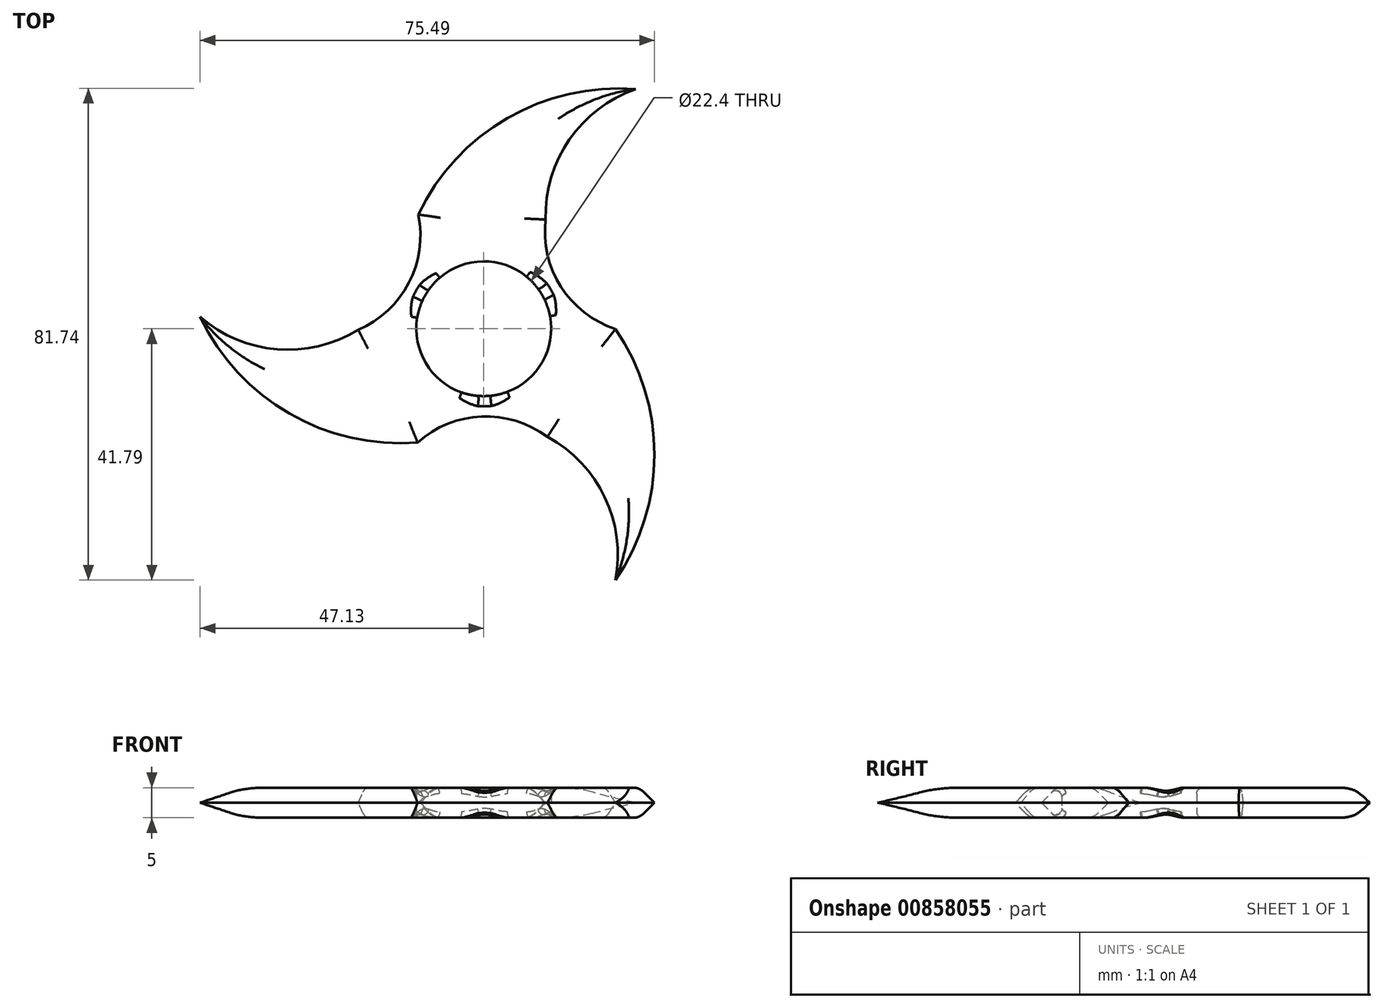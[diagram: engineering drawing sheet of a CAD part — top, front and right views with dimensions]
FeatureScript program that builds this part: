
annotation { "Feature Type Name" : "Feature", "Feature Type Description" : "" }
export const myFeature = defineFeature(function(context is Context, id is Id, definition is map)
    precondition{}
    {
        {
            var Q0;
            Q0=qCreatedBy(makeId("Top.planeOp"),FACE);
            var sketch = newSketch(context, id + "F0", { "sketchPlane" : qUnion([Q0])});
            skCircle(sketch, "E0", {"center": v(0, 0) * mm, "radius": 11.2 * mm});
            skArc(sketch, "E1", {"start": v(10.29, 18.16) * mm, "mid": v(12.82, 6.98) * mm, "end": v(21.87, -0.05) * mm});
            skArc(sketch, "E2.1.0", {"start": v(-20.87, -0.17) * mm, "mid": v(-12.45, 7.61) * mm, "end": v(-10.9, 18.97) * mm});
            skArc(sketch, "E2.2.0", {"start": v(10.58, -17.99) * mm, "mid": v(-0.37, -14.6) * mm, "end": v(-10.98, -18.92) * mm});
            skArc(sketch, "E3", {"start": v(21.87, -41.8) * mm, "mid": v(28.36, -20.92) * mm, "end": v(21.87, -0.05) * mm});
            skArc(sketch, "E4", {"start": v(21.87, -41.8) * mm, "mid": v(20.12, -28.04) * mm, "end": v(10.58, -17.99) * mm});
            skPoint(sketch, "E5.center.orphan", {"position": v(0, 26.43) * mm});
            skArc(sketch, "E6.1.0", {"start": v(25.26, 39.84) * mm, "mid": v(3.94, 35.02) * mm, "end": v(-10.9, 18.97) * mm});
            skArc(sketch, "E6.1.1", {"start": v(25.26, 39.84) * mm, "mid": v(14.22, 31.45) * mm, "end": v(10.29, 18.16) * mm});
            skArc(sketch, "E6.2.0", {"start": v(-47.13, 1.95) * mm, "mid": v(-32.3, -14.1) * mm, "end": v(-10.98, -18.92) * mm});
            skArc(sketch, "E6.2.1", {"start": v(-47.13, 1.95) * mm, "mid": v(-34.35, -3.4) * mm, "end": v(-20.87, -0.17) * mm});
            skSolve(sketch);
        }
        {
            var Q0;
            Q0 = qSketchRegion(id + "F0", true);
            extrude(context, id + "F1", {"entities" : qUnion([Q0]), "depth" : 2.5 * mm, "offsetDistance" : 25 * mm, "hasSecondDirection" : true, "secondDirectionOppositeDirection" : true, "secondDirectionDepth" : 2.5 * mm});
        }
        {
            var Q0;
            Q0=makeQuery(id+"F1.opExtrude","CAP_EDGE",EDGE,{"disambiguationData":[OSD([sQuery(id+"F0.wireOp",EDGE,"E3")])],"isStart":false});
            var Q1;
            Q1=makeQuery(id+"F1.opExtrude","CAP_EDGE",EDGE,{"disambiguationData":[OSD([sQuery(id+"F0.wireOp",EDGE,"E6.1.1")])],"isStart":false});
            var Q2;
            Q2=makeQuery(id+"F1.opExtrude","CAP_EDGE",EDGE,{"disambiguationData":[OSD([sQuery(id+"F0.wireOp",EDGE,"E6.1.0")])],"isStart":false});
            var Q3;
            Q3=makeQuery(id+"F1.opExtrude","CAP_EDGE",EDGE,{"disambiguationData":[OSD([sQuery(id+"F0.wireOp",EDGE,"E1")])],"isStart":false});
            var Q4;
            Q4=makeQuery(id+"F1.opExtrude","CAP_EDGE",EDGE,{"disambiguationData":[OSD([sQuery(id+"F0.wireOp",EDGE,"E2.2.0")])],"isStart":false});
            var Q5;
            Q5=makeQuery(id+"F1.opExtrude","CAP_EDGE",EDGE,{"disambiguationData":[OSD([sQuery(id+"F0.wireOp",EDGE,"E4")])],"isStart":false});
            var Q6;
            Q6=makeQuery(id+"F1.opExtrude","CAP_EDGE",EDGE,{"disambiguationData":[OSD([sQuery(id+"F0.wireOp",EDGE,"E6.2.1")])],"isStart":false});
            var Q7;
            Q7=makeQuery(id+"F1.opExtrude","CAP_EDGE",EDGE,{"disambiguationData":[OSD([sQuery(id+"F0.wireOp",EDGE,"E2.1.0")])],"isStart":false});
            var Q8;
            Q8=makeQuery(id+"F1.opExtrude","CAP_EDGE",EDGE,{"disambiguationData":[OSD([sQuery(id+"F0.wireOp",EDGE,"E6.2.0")])],"isStart":false});
            chamfer(context, id + "F2", {"entities" : qUnion([Q0, Q1, Q2, Q3, Q4, Q5, Q6, Q7, Q8]), "width" : 2.5 * mm, "tangentPropagation" : true});
        }
        {
            var Q0;
            Q0=makeQuery(id+"F1.opExtrude","CAP_EDGE",EDGE,{"disambiguationData":[OSD([sQuery(id+"F0.wireOp",EDGE,"E6.2.0")])],"isStart":true});
            var Q1;
            Q1=makeQuery(id+"F1.opExtrude","CAP_EDGE",EDGE,{"disambiguationData":[OSD([sQuery(id+"F0.wireOp",EDGE,"E2.2.0")])],"isStart":true});
            var Q2;
            Q2=makeQuery(id+"F1.opExtrude","CAP_EDGE",EDGE,{"disambiguationData":[OSD([sQuery(id+"F0.wireOp",EDGE,"E4")])],"isStart":true});
            var Q3;
            Q3=makeQuery(id+"F1.opExtrude","CAP_EDGE",EDGE,{"disambiguationData":[OSD([sQuery(id+"F0.wireOp",EDGE,"E3")])],"isStart":true});
            var Q4;
            Q4=makeQuery(id+"F1.opExtrude","CAP_EDGE",EDGE,{"disambiguationData":[OSD([sQuery(id+"F0.wireOp",EDGE,"E1")])],"isStart":true});
            var Q5;
            Q5=makeQuery(id+"F1.opExtrude","CAP_EDGE",EDGE,{"disambiguationData":[OSD([sQuery(id+"F0.wireOp",EDGE,"E6.1.1")])],"isStart":true});
            var Q6;
            Q6=makeQuery(id+"F1.opExtrude","CAP_EDGE",EDGE,{"disambiguationData":[OSD([sQuery(id+"F0.wireOp",EDGE,"E6.1.0")])],"isStart":true});
            var Q7;
            Q7=makeQuery(id+"F1.opExtrude","CAP_EDGE",EDGE,{"disambiguationData":[OSD([sQuery(id+"F0.wireOp",EDGE,"E2.1.0")])],"isStart":true});
            var Q8;
            Q8=makeQuery(id+"F1.opExtrude","CAP_EDGE",EDGE,{"disambiguationData":[OSD([sQuery(id+"F0.wireOp",EDGE,"E6.2.1")])],"isStart":true});
            chamfer(context, id + "F3", {"entities" : qUnion([Q0, Q1, Q2, Q3, Q4, Q5, Q6, Q7, Q8]), "width" : 2.5 * mm, "tangentPropagation" : true});
        }
        {
            var Q0;
            {var subQ0=sQuery(id+"F0.wireOp",EDGE,"E6.2.0");Q0=makeQuery(id+"F3.opChamfer","BLEND_EDGE",EDGE,{"blendedFrom":[makeQuery(id+"F1.opExtrude","CAP_EDGE",EDGE,{"disambiguationData":[OSD([subQ0])],"isStart":true}),makeQuery(id+"F1.opExtrude","CAP_FACE",FACE,{"disambiguationData":[OSD([sQuery(id+"F0.wireOp",EDGE,"E0"),sQuery(id+"F0.wireOp",EDGE,"E1"),sQuery(id+"F0.wireOp",EDGE,"E2.1.0"),sQuery(id+"F0.wireOp",EDGE,"E2.2.0"),sQuery(id+"F0.wireOp",EDGE,"E3"),sQuery(id+"F0.wireOp",EDGE,"E4"),sQuery(id+"F0.wireOp",EDGE,"E6.1.0"),sQuery(id+"F0.wireOp",EDGE,"E6.1.1"),subQ0,sQuery(id+"F0.wireOp",EDGE,"E6.2.1")])],"isStart":true})],"blendedInto":[makeQuery(id+"F1.opExtrude","CAP_FACE",FACE,{"disambiguationData":[OSD([sQuery(id+"F0.wireOp",EDGE,"E0"),sQuery(id+"F0.wireOp",EDGE,"E1"),sQuery(id+"F0.wireOp",EDGE,"E2.1.0"),sQuery(id+"F0.wireOp",EDGE,"E2.2.0"),sQuery(id+"F0.wireOp",EDGE,"E3"),sQuery(id+"F0.wireOp",EDGE,"E4"),sQuery(id+"F0.wireOp",EDGE,"E6.1.0"),sQuery(id+"F0.wireOp",EDGE,"E6.1.1"),subQ0,sQuery(id+"F0.wireOp",EDGE,"E6.2.1")])],"isStart":true})]});}
            var Q1;
            {var subQ0=sQuery(id+"F0.wireOp",EDGE,"E6.2.1");Q1=makeQuery(id+"F3.opChamfer","BLEND_EDGE",EDGE,{"blendedFrom":[makeQuery(id+"F1.opExtrude","CAP_EDGE",EDGE,{"disambiguationData":[OSD([subQ0])],"isStart":true}),makeQuery(id+"F1.opExtrude","CAP_FACE",FACE,{"disambiguationData":[OSD([sQuery(id+"F0.wireOp",EDGE,"E0"),sQuery(id+"F0.wireOp",EDGE,"E1"),sQuery(id+"F0.wireOp",EDGE,"E2.1.0"),sQuery(id+"F0.wireOp",EDGE,"E2.2.0"),sQuery(id+"F0.wireOp",EDGE,"E3"),sQuery(id+"F0.wireOp",EDGE,"E4"),sQuery(id+"F0.wireOp",EDGE,"E6.1.0"),sQuery(id+"F0.wireOp",EDGE,"E6.1.1"),sQuery(id+"F0.wireOp",EDGE,"E6.2.0"),subQ0])],"isStart":true})],"blendedInto":[makeQuery(id+"F1.opExtrude","CAP_FACE",FACE,{"disambiguationData":[OSD([sQuery(id+"F0.wireOp",EDGE,"E0"),sQuery(id+"F0.wireOp",EDGE,"E1"),sQuery(id+"F0.wireOp",EDGE,"E2.1.0"),sQuery(id+"F0.wireOp",EDGE,"E2.2.0"),sQuery(id+"F0.wireOp",EDGE,"E3"),sQuery(id+"F0.wireOp",EDGE,"E4"),sQuery(id+"F0.wireOp",EDGE,"E6.1.0"),sQuery(id+"F0.wireOp",EDGE,"E6.1.1"),sQuery(id+"F0.wireOp",EDGE,"E6.2.0"),subQ0])],"isStart":true})]});}
            var Q2;
            {var subQ0=sQuery(id+"F0.wireOp",EDGE,"E2.1.0");Q2=makeQuery(id+"F3.opChamfer","BLEND_EDGE",EDGE,{"blendedFrom":[makeQuery(id+"F1.opExtrude","CAP_EDGE",EDGE,{"disambiguationData":[OSD([subQ0])],"isStart":true}),makeQuery(id+"F1.opExtrude","CAP_FACE",FACE,{"disambiguationData":[OSD([sQuery(id+"F0.wireOp",EDGE,"E0"),sQuery(id+"F0.wireOp",EDGE,"E1"),subQ0,sQuery(id+"F0.wireOp",EDGE,"E2.2.0"),sQuery(id+"F0.wireOp",EDGE,"E3"),sQuery(id+"F0.wireOp",EDGE,"E4"),sQuery(id+"F0.wireOp",EDGE,"E6.1.0"),sQuery(id+"F0.wireOp",EDGE,"E6.1.1"),sQuery(id+"F0.wireOp",EDGE,"E6.2.0"),sQuery(id+"F0.wireOp",EDGE,"E6.2.1")])],"isStart":true})],"blendedInto":[makeQuery(id+"F1.opExtrude","CAP_FACE",FACE,{"disambiguationData":[OSD([sQuery(id+"F0.wireOp",EDGE,"E0"),sQuery(id+"F0.wireOp",EDGE,"E1"),subQ0,sQuery(id+"F0.wireOp",EDGE,"E2.2.0"),sQuery(id+"F0.wireOp",EDGE,"E3"),sQuery(id+"F0.wireOp",EDGE,"E4"),sQuery(id+"F0.wireOp",EDGE,"E6.1.0"),sQuery(id+"F0.wireOp",EDGE,"E6.1.1"),sQuery(id+"F0.wireOp",EDGE,"E6.2.0"),sQuery(id+"F0.wireOp",EDGE,"E6.2.1")])],"isStart":true})]});}
            var Q3;
            {var subQ0=sQuery(id+"F0.wireOp",EDGE,"E2.2.0");Q3=makeQuery(id+"F3.opChamfer","BLEND_EDGE",EDGE,{"blendedFrom":[makeQuery(id+"F1.opExtrude","CAP_EDGE",EDGE,{"disambiguationData":[OSD([subQ0])],"isStart":true}),makeQuery(id+"F1.opExtrude","CAP_FACE",FACE,{"disambiguationData":[OSD([sQuery(id+"F0.wireOp",EDGE,"E0"),sQuery(id+"F0.wireOp",EDGE,"E1"),sQuery(id+"F0.wireOp",EDGE,"E2.1.0"),subQ0,sQuery(id+"F0.wireOp",EDGE,"E3"),sQuery(id+"F0.wireOp",EDGE,"E4"),sQuery(id+"F0.wireOp",EDGE,"E6.1.0"),sQuery(id+"F0.wireOp",EDGE,"E6.1.1"),sQuery(id+"F0.wireOp",EDGE,"E6.2.0"),sQuery(id+"F0.wireOp",EDGE,"E6.2.1")])],"isStart":true})],"blendedInto":[makeQuery(id+"F1.opExtrude","CAP_FACE",FACE,{"disambiguationData":[OSD([sQuery(id+"F0.wireOp",EDGE,"E0"),sQuery(id+"F0.wireOp",EDGE,"E1"),sQuery(id+"F0.wireOp",EDGE,"E2.1.0"),subQ0,sQuery(id+"F0.wireOp",EDGE,"E3"),sQuery(id+"F0.wireOp",EDGE,"E4"),sQuery(id+"F0.wireOp",EDGE,"E6.1.0"),sQuery(id+"F0.wireOp",EDGE,"E6.1.1"),sQuery(id+"F0.wireOp",EDGE,"E6.2.0"),sQuery(id+"F0.wireOp",EDGE,"E6.2.1")])],"isStart":true})]});}
            var Q4;
            {var subQ0=sQuery(id+"F0.wireOp",EDGE,"E4");Q4=makeQuery(id+"F3.opChamfer","BLEND_EDGE",EDGE,{"blendedFrom":[makeQuery(id+"F1.opExtrude","CAP_EDGE",EDGE,{"disambiguationData":[OSD([subQ0])],"isStart":true}),makeQuery(id+"F1.opExtrude","CAP_FACE",FACE,{"disambiguationData":[OSD([sQuery(id+"F0.wireOp",EDGE,"E0"),sQuery(id+"F0.wireOp",EDGE,"E1"),sQuery(id+"F0.wireOp",EDGE,"E2.1.0"),sQuery(id+"F0.wireOp",EDGE,"E2.2.0"),sQuery(id+"F0.wireOp",EDGE,"E3"),subQ0,sQuery(id+"F0.wireOp",EDGE,"E6.1.0"),sQuery(id+"F0.wireOp",EDGE,"E6.1.1"),sQuery(id+"F0.wireOp",EDGE,"E6.2.0"),sQuery(id+"F0.wireOp",EDGE,"E6.2.1")])],"isStart":true})],"blendedInto":[makeQuery(id+"F1.opExtrude","CAP_FACE",FACE,{"disambiguationData":[OSD([sQuery(id+"F0.wireOp",EDGE,"E0"),sQuery(id+"F0.wireOp",EDGE,"E1"),sQuery(id+"F0.wireOp",EDGE,"E2.1.0"),sQuery(id+"F0.wireOp",EDGE,"E2.2.0"),sQuery(id+"F0.wireOp",EDGE,"E3"),subQ0,sQuery(id+"F0.wireOp",EDGE,"E6.1.0"),sQuery(id+"F0.wireOp",EDGE,"E6.1.1"),sQuery(id+"F0.wireOp",EDGE,"E6.2.0"),sQuery(id+"F0.wireOp",EDGE,"E6.2.1")])],"isStart":true})]});}
            var Q5;
            {var subQ0=sQuery(id+"F0.wireOp",EDGE,"E3");Q5=makeQuery(id+"F3.opChamfer","BLEND_EDGE",EDGE,{"blendedFrom":[makeQuery(id+"F1.opExtrude","CAP_EDGE",EDGE,{"disambiguationData":[OSD([subQ0])],"isStart":true}),makeQuery(id+"F1.opExtrude","CAP_FACE",FACE,{"disambiguationData":[OSD([sQuery(id+"F0.wireOp",EDGE,"E0"),sQuery(id+"F0.wireOp",EDGE,"E1"),sQuery(id+"F0.wireOp",EDGE,"E2.1.0"),sQuery(id+"F0.wireOp",EDGE,"E2.2.0"),subQ0,sQuery(id+"F0.wireOp",EDGE,"E4"),sQuery(id+"F0.wireOp",EDGE,"E6.1.0"),sQuery(id+"F0.wireOp",EDGE,"E6.1.1"),sQuery(id+"F0.wireOp",EDGE,"E6.2.0"),sQuery(id+"F0.wireOp",EDGE,"E6.2.1")])],"isStart":true})],"blendedInto":[makeQuery(id+"F1.opExtrude","CAP_FACE",FACE,{"disambiguationData":[OSD([sQuery(id+"F0.wireOp",EDGE,"E0"),sQuery(id+"F0.wireOp",EDGE,"E1"),sQuery(id+"F0.wireOp",EDGE,"E2.1.0"),sQuery(id+"F0.wireOp",EDGE,"E2.2.0"),subQ0,sQuery(id+"F0.wireOp",EDGE,"E4"),sQuery(id+"F0.wireOp",EDGE,"E6.1.0"),sQuery(id+"F0.wireOp",EDGE,"E6.1.1"),sQuery(id+"F0.wireOp",EDGE,"E6.2.0"),sQuery(id+"F0.wireOp",EDGE,"E6.2.1")])],"isStart":true})]});}
            var Q6;
            {var subQ0=sQuery(id+"F0.wireOp",EDGE,"E1");Q6=makeQuery(id+"F3.opChamfer","BLEND_EDGE",EDGE,{"blendedFrom":[makeQuery(id+"F1.opExtrude","CAP_EDGE",EDGE,{"disambiguationData":[OSD([subQ0])],"isStart":true}),makeQuery(id+"F1.opExtrude","CAP_FACE",FACE,{"disambiguationData":[OSD([sQuery(id+"F0.wireOp",EDGE,"E0"),subQ0,sQuery(id+"F0.wireOp",EDGE,"E2.1.0"),sQuery(id+"F0.wireOp",EDGE,"E2.2.0"),sQuery(id+"F0.wireOp",EDGE,"E3"),sQuery(id+"F0.wireOp",EDGE,"E4"),sQuery(id+"F0.wireOp",EDGE,"E6.1.0"),sQuery(id+"F0.wireOp",EDGE,"E6.1.1"),sQuery(id+"F0.wireOp",EDGE,"E6.2.0"),sQuery(id+"F0.wireOp",EDGE,"E6.2.1")])],"isStart":true})],"blendedInto":[makeQuery(id+"F1.opExtrude","CAP_FACE",FACE,{"disambiguationData":[OSD([sQuery(id+"F0.wireOp",EDGE,"E0"),subQ0,sQuery(id+"F0.wireOp",EDGE,"E2.1.0"),sQuery(id+"F0.wireOp",EDGE,"E2.2.0"),sQuery(id+"F0.wireOp",EDGE,"E3"),sQuery(id+"F0.wireOp",EDGE,"E4"),sQuery(id+"F0.wireOp",EDGE,"E6.1.0"),sQuery(id+"F0.wireOp",EDGE,"E6.1.1"),sQuery(id+"F0.wireOp",EDGE,"E6.2.0"),sQuery(id+"F0.wireOp",EDGE,"E6.2.1")])],"isStart":true})]});}
            var Q7;
            {var subQ0=sQuery(id+"F0.wireOp",EDGE,"E6.1.1");Q7=makeQuery(id+"F3.opChamfer","BLEND_EDGE",EDGE,{"blendedFrom":[makeQuery(id+"F1.opExtrude","CAP_EDGE",EDGE,{"disambiguationData":[OSD([subQ0])],"isStart":true}),makeQuery(id+"F1.opExtrude","CAP_FACE",FACE,{"disambiguationData":[OSD([sQuery(id+"F0.wireOp",EDGE,"E0"),sQuery(id+"F0.wireOp",EDGE,"E1"),sQuery(id+"F0.wireOp",EDGE,"E2.1.0"),sQuery(id+"F0.wireOp",EDGE,"E2.2.0"),sQuery(id+"F0.wireOp",EDGE,"E3"),sQuery(id+"F0.wireOp",EDGE,"E4"),sQuery(id+"F0.wireOp",EDGE,"E6.1.0"),subQ0,sQuery(id+"F0.wireOp",EDGE,"E6.2.0"),sQuery(id+"F0.wireOp",EDGE,"E6.2.1")])],"isStart":true})],"blendedInto":[makeQuery(id+"F1.opExtrude","CAP_FACE",FACE,{"disambiguationData":[OSD([sQuery(id+"F0.wireOp",EDGE,"E0"),sQuery(id+"F0.wireOp",EDGE,"E1"),sQuery(id+"F0.wireOp",EDGE,"E2.1.0"),sQuery(id+"F0.wireOp",EDGE,"E2.2.0"),sQuery(id+"F0.wireOp",EDGE,"E3"),sQuery(id+"F0.wireOp",EDGE,"E4"),sQuery(id+"F0.wireOp",EDGE,"E6.1.0"),subQ0,sQuery(id+"F0.wireOp",EDGE,"E6.2.0"),sQuery(id+"F0.wireOp",EDGE,"E6.2.1")])],"isStart":true})]});}
            var Q8;
            {var subQ0=sQuery(id+"F0.wireOp",EDGE,"E6.1.0");Q8=makeQuery(id+"F3.opChamfer","BLEND_EDGE",EDGE,{"blendedFrom":[makeQuery(id+"F1.opExtrude","CAP_EDGE",EDGE,{"disambiguationData":[OSD([subQ0])],"isStart":true}),makeQuery(id+"F1.opExtrude","CAP_FACE",FACE,{"disambiguationData":[OSD([sQuery(id+"F0.wireOp",EDGE,"E0"),sQuery(id+"F0.wireOp",EDGE,"E1"),sQuery(id+"F0.wireOp",EDGE,"E2.1.0"),sQuery(id+"F0.wireOp",EDGE,"E2.2.0"),sQuery(id+"F0.wireOp",EDGE,"E3"),sQuery(id+"F0.wireOp",EDGE,"E4"),subQ0,sQuery(id+"F0.wireOp",EDGE,"E6.1.1"),sQuery(id+"F0.wireOp",EDGE,"E6.2.0"),sQuery(id+"F0.wireOp",EDGE,"E6.2.1")])],"isStart":true})],"blendedInto":[makeQuery(id+"F1.opExtrude","CAP_FACE",FACE,{"disambiguationData":[OSD([sQuery(id+"F0.wireOp",EDGE,"E0"),sQuery(id+"F0.wireOp",EDGE,"E1"),sQuery(id+"F0.wireOp",EDGE,"E2.1.0"),sQuery(id+"F0.wireOp",EDGE,"E2.2.0"),sQuery(id+"F0.wireOp",EDGE,"E3"),sQuery(id+"F0.wireOp",EDGE,"E4"),subQ0,sQuery(id+"F0.wireOp",EDGE,"E6.1.1"),sQuery(id+"F0.wireOp",EDGE,"E6.2.0"),sQuery(id+"F0.wireOp",EDGE,"E6.2.1")])],"isStart":true})]});}
            fillet(context, id + "F4", {"entities" : qUnion([Q0, Q1, Q2, Q3, Q4, Q5, Q6, Q7, Q8]), "radius" : 2.5 * mm, "tangentPropagation" : true, "allowEdgeOverflow" : false});
        }
        {
            var Q0;
            {var subQ0=sQuery(id+"F0.wireOp",EDGE,"E4");Q0=makeQuery(id+"F2.opChamfer","BLEND_EDGE",EDGE,{"blendedFrom":[makeQuery(id+"F1.opExtrude","CAP_EDGE",EDGE,{"disambiguationData":[OSD([subQ0])],"isStart":false}),makeQuery(id+"F1.opExtrude","CAP_FACE",FACE,{"disambiguationData":[OSD([sQuery(id+"F0.wireOp",EDGE,"E0"),sQuery(id+"F0.wireOp",EDGE,"E1"),sQuery(id+"F0.wireOp",EDGE,"E2.1.0"),sQuery(id+"F0.wireOp",EDGE,"E2.2.0"),sQuery(id+"F0.wireOp",EDGE,"E3"),subQ0,sQuery(id+"F0.wireOp",EDGE,"E6.1.0"),sQuery(id+"F0.wireOp",EDGE,"E6.1.1"),sQuery(id+"F0.wireOp",EDGE,"E6.2.0"),sQuery(id+"F0.wireOp",EDGE,"E6.2.1")])],"isStart":false})],"blendedInto":[makeQuery(id+"F1.opExtrude","CAP_FACE",FACE,{"disambiguationData":[OSD([sQuery(id+"F0.wireOp",EDGE,"E0"),sQuery(id+"F0.wireOp",EDGE,"E1"),sQuery(id+"F0.wireOp",EDGE,"E2.1.0"),sQuery(id+"F0.wireOp",EDGE,"E2.2.0"),sQuery(id+"F0.wireOp",EDGE,"E3"),subQ0,sQuery(id+"F0.wireOp",EDGE,"E6.1.0"),sQuery(id+"F0.wireOp",EDGE,"E6.1.1"),sQuery(id+"F0.wireOp",EDGE,"E6.2.0"),sQuery(id+"F0.wireOp",EDGE,"E6.2.1")])],"isStart":false})]});}
            var Q1;
            {var subQ0=sQuery(id+"F0.wireOp",EDGE,"E3");Q1=makeQuery(id+"F2.opChamfer","BLEND_EDGE",EDGE,{"blendedFrom":[makeQuery(id+"F1.opExtrude","CAP_EDGE",EDGE,{"disambiguationData":[OSD([subQ0])],"isStart":false}),makeQuery(id+"F1.opExtrude","CAP_FACE",FACE,{"disambiguationData":[OSD([sQuery(id+"F0.wireOp",EDGE,"E0"),sQuery(id+"F0.wireOp",EDGE,"E1"),sQuery(id+"F0.wireOp",EDGE,"E2.1.0"),sQuery(id+"F0.wireOp",EDGE,"E2.2.0"),subQ0,sQuery(id+"F0.wireOp",EDGE,"E4"),sQuery(id+"F0.wireOp",EDGE,"E6.1.0"),sQuery(id+"F0.wireOp",EDGE,"E6.1.1"),sQuery(id+"F0.wireOp",EDGE,"E6.2.0"),sQuery(id+"F0.wireOp",EDGE,"E6.2.1")])],"isStart":false})],"blendedInto":[makeQuery(id+"F1.opExtrude","CAP_FACE",FACE,{"disambiguationData":[OSD([sQuery(id+"F0.wireOp",EDGE,"E0"),sQuery(id+"F0.wireOp",EDGE,"E1"),sQuery(id+"F0.wireOp",EDGE,"E2.1.0"),sQuery(id+"F0.wireOp",EDGE,"E2.2.0"),subQ0,sQuery(id+"F0.wireOp",EDGE,"E4"),sQuery(id+"F0.wireOp",EDGE,"E6.1.0"),sQuery(id+"F0.wireOp",EDGE,"E6.1.1"),sQuery(id+"F0.wireOp",EDGE,"E6.2.0"),sQuery(id+"F0.wireOp",EDGE,"E6.2.1")])],"isStart":false})]});}
            var Q2;
            {var subQ0=sQuery(id+"F0.wireOp",EDGE,"E2.2.0");Q2=makeQuery(id+"F2.opChamfer","BLEND_EDGE",EDGE,{"blendedFrom":[makeQuery(id+"F1.opExtrude","CAP_EDGE",EDGE,{"disambiguationData":[OSD([subQ0])],"isStart":false}),makeQuery(id+"F1.opExtrude","CAP_FACE",FACE,{"disambiguationData":[OSD([sQuery(id+"F0.wireOp",EDGE,"E0"),sQuery(id+"F0.wireOp",EDGE,"E1"),sQuery(id+"F0.wireOp",EDGE,"E2.1.0"),subQ0,sQuery(id+"F0.wireOp",EDGE,"E3"),sQuery(id+"F0.wireOp",EDGE,"E4"),sQuery(id+"F0.wireOp",EDGE,"E6.1.0"),sQuery(id+"F0.wireOp",EDGE,"E6.1.1"),sQuery(id+"F0.wireOp",EDGE,"E6.2.0"),sQuery(id+"F0.wireOp",EDGE,"E6.2.1")])],"isStart":false})],"blendedInto":[makeQuery(id+"F1.opExtrude","CAP_FACE",FACE,{"disambiguationData":[OSD([sQuery(id+"F0.wireOp",EDGE,"E0"),sQuery(id+"F0.wireOp",EDGE,"E1"),sQuery(id+"F0.wireOp",EDGE,"E2.1.0"),subQ0,sQuery(id+"F0.wireOp",EDGE,"E3"),sQuery(id+"F0.wireOp",EDGE,"E4"),sQuery(id+"F0.wireOp",EDGE,"E6.1.0"),sQuery(id+"F0.wireOp",EDGE,"E6.1.1"),sQuery(id+"F0.wireOp",EDGE,"E6.2.0"),sQuery(id+"F0.wireOp",EDGE,"E6.2.1")])],"isStart":false})]});}
            var Q3;
            {var subQ0=sQuery(id+"F0.wireOp",EDGE,"E6.2.0");Q3=makeQuery(id+"F2.opChamfer","BLEND_EDGE",EDGE,{"blendedFrom":[makeQuery(id+"F1.opExtrude","CAP_EDGE",EDGE,{"disambiguationData":[OSD([subQ0])],"isStart":false}),makeQuery(id+"F1.opExtrude","CAP_FACE",FACE,{"disambiguationData":[OSD([sQuery(id+"F0.wireOp",EDGE,"E0"),sQuery(id+"F0.wireOp",EDGE,"E1"),sQuery(id+"F0.wireOp",EDGE,"E2.1.0"),sQuery(id+"F0.wireOp",EDGE,"E2.2.0"),sQuery(id+"F0.wireOp",EDGE,"E3"),sQuery(id+"F0.wireOp",EDGE,"E4"),sQuery(id+"F0.wireOp",EDGE,"E6.1.0"),sQuery(id+"F0.wireOp",EDGE,"E6.1.1"),subQ0,sQuery(id+"F0.wireOp",EDGE,"E6.2.1")])],"isStart":false})],"blendedInto":[makeQuery(id+"F1.opExtrude","CAP_FACE",FACE,{"disambiguationData":[OSD([sQuery(id+"F0.wireOp",EDGE,"E0"),sQuery(id+"F0.wireOp",EDGE,"E1"),sQuery(id+"F0.wireOp",EDGE,"E2.1.0"),sQuery(id+"F0.wireOp",EDGE,"E2.2.0"),sQuery(id+"F0.wireOp",EDGE,"E3"),sQuery(id+"F0.wireOp",EDGE,"E4"),sQuery(id+"F0.wireOp",EDGE,"E6.1.0"),sQuery(id+"F0.wireOp",EDGE,"E6.1.1"),subQ0,sQuery(id+"F0.wireOp",EDGE,"E6.2.1")])],"isStart":false})]});}
            var Q4;
            {var subQ0=sQuery(id+"F0.wireOp",EDGE,"E6.2.1");Q4=makeQuery(id+"F2.opChamfer","BLEND_EDGE",EDGE,{"blendedFrom":[makeQuery(id+"F1.opExtrude","CAP_EDGE",EDGE,{"disambiguationData":[OSD([subQ0])],"isStart":false}),makeQuery(id+"F1.opExtrude","CAP_FACE",FACE,{"disambiguationData":[OSD([sQuery(id+"F0.wireOp",EDGE,"E0"),sQuery(id+"F0.wireOp",EDGE,"E1"),sQuery(id+"F0.wireOp",EDGE,"E2.1.0"),sQuery(id+"F0.wireOp",EDGE,"E2.2.0"),sQuery(id+"F0.wireOp",EDGE,"E3"),sQuery(id+"F0.wireOp",EDGE,"E4"),sQuery(id+"F0.wireOp",EDGE,"E6.1.0"),sQuery(id+"F0.wireOp",EDGE,"E6.1.1"),sQuery(id+"F0.wireOp",EDGE,"E6.2.0"),subQ0])],"isStart":false})],"blendedInto":[makeQuery(id+"F1.opExtrude","CAP_FACE",FACE,{"disambiguationData":[OSD([sQuery(id+"F0.wireOp",EDGE,"E0"),sQuery(id+"F0.wireOp",EDGE,"E1"),sQuery(id+"F0.wireOp",EDGE,"E2.1.0"),sQuery(id+"F0.wireOp",EDGE,"E2.2.0"),sQuery(id+"F0.wireOp",EDGE,"E3"),sQuery(id+"F0.wireOp",EDGE,"E4"),sQuery(id+"F0.wireOp",EDGE,"E6.1.0"),sQuery(id+"F0.wireOp",EDGE,"E6.1.1"),sQuery(id+"F0.wireOp",EDGE,"E6.2.0"),subQ0])],"isStart":false})]});}
            var Q5;
            {var subQ0=sQuery(id+"F0.wireOp",EDGE,"E2.1.0");Q5=makeQuery(id+"F2.opChamfer","BLEND_EDGE",EDGE,{"blendedFrom":[makeQuery(id+"F1.opExtrude","CAP_EDGE",EDGE,{"disambiguationData":[OSD([subQ0])],"isStart":false}),makeQuery(id+"F1.opExtrude","CAP_FACE",FACE,{"disambiguationData":[OSD([sQuery(id+"F0.wireOp",EDGE,"E0"),sQuery(id+"F0.wireOp",EDGE,"E1"),subQ0,sQuery(id+"F0.wireOp",EDGE,"E2.2.0"),sQuery(id+"F0.wireOp",EDGE,"E3"),sQuery(id+"F0.wireOp",EDGE,"E4"),sQuery(id+"F0.wireOp",EDGE,"E6.1.0"),sQuery(id+"F0.wireOp",EDGE,"E6.1.1"),sQuery(id+"F0.wireOp",EDGE,"E6.2.0"),sQuery(id+"F0.wireOp",EDGE,"E6.2.1")])],"isStart":false})],"blendedInto":[makeQuery(id+"F1.opExtrude","CAP_FACE",FACE,{"disambiguationData":[OSD([sQuery(id+"F0.wireOp",EDGE,"E0"),sQuery(id+"F0.wireOp",EDGE,"E1"),subQ0,sQuery(id+"F0.wireOp",EDGE,"E2.2.0"),sQuery(id+"F0.wireOp",EDGE,"E3"),sQuery(id+"F0.wireOp",EDGE,"E4"),sQuery(id+"F0.wireOp",EDGE,"E6.1.0"),sQuery(id+"F0.wireOp",EDGE,"E6.1.1"),sQuery(id+"F0.wireOp",EDGE,"E6.2.0"),sQuery(id+"F0.wireOp",EDGE,"E6.2.1")])],"isStart":false})]});}
            var Q6;
            {var subQ0=sQuery(id+"F0.wireOp",EDGE,"E6.1.0");Q6=makeQuery(id+"F2.opChamfer","BLEND_EDGE",EDGE,{"blendedFrom":[makeQuery(id+"F1.opExtrude","CAP_EDGE",EDGE,{"disambiguationData":[OSD([subQ0])],"isStart":false}),makeQuery(id+"F1.opExtrude","CAP_FACE",FACE,{"disambiguationData":[OSD([sQuery(id+"F0.wireOp",EDGE,"E0"),sQuery(id+"F0.wireOp",EDGE,"E1"),sQuery(id+"F0.wireOp",EDGE,"E2.1.0"),sQuery(id+"F0.wireOp",EDGE,"E2.2.0"),sQuery(id+"F0.wireOp",EDGE,"E3"),sQuery(id+"F0.wireOp",EDGE,"E4"),subQ0,sQuery(id+"F0.wireOp",EDGE,"E6.1.1"),sQuery(id+"F0.wireOp",EDGE,"E6.2.0"),sQuery(id+"F0.wireOp",EDGE,"E6.2.1")])],"isStart":false})],"blendedInto":[makeQuery(id+"F1.opExtrude","CAP_FACE",FACE,{"disambiguationData":[OSD([sQuery(id+"F0.wireOp",EDGE,"E0"),sQuery(id+"F0.wireOp",EDGE,"E1"),sQuery(id+"F0.wireOp",EDGE,"E2.1.0"),sQuery(id+"F0.wireOp",EDGE,"E2.2.0"),sQuery(id+"F0.wireOp",EDGE,"E3"),sQuery(id+"F0.wireOp",EDGE,"E4"),subQ0,sQuery(id+"F0.wireOp",EDGE,"E6.1.1"),sQuery(id+"F0.wireOp",EDGE,"E6.2.0"),sQuery(id+"F0.wireOp",EDGE,"E6.2.1")])],"isStart":false})]});}
            var Q7;
            {var subQ0=sQuery(id+"F0.wireOp",EDGE,"E1");Q7=makeQuery(id+"F2.opChamfer","BLEND_EDGE",EDGE,{"blendedFrom":[makeQuery(id+"F1.opExtrude","CAP_EDGE",EDGE,{"disambiguationData":[OSD([subQ0])],"isStart":false}),makeQuery(id+"F1.opExtrude","CAP_FACE",FACE,{"disambiguationData":[OSD([sQuery(id+"F0.wireOp",EDGE,"E0"),subQ0,sQuery(id+"F0.wireOp",EDGE,"E2.1.0"),sQuery(id+"F0.wireOp",EDGE,"E2.2.0"),sQuery(id+"F0.wireOp",EDGE,"E3"),sQuery(id+"F0.wireOp",EDGE,"E4"),sQuery(id+"F0.wireOp",EDGE,"E6.1.0"),sQuery(id+"F0.wireOp",EDGE,"E6.1.1"),sQuery(id+"F0.wireOp",EDGE,"E6.2.0"),sQuery(id+"F0.wireOp",EDGE,"E6.2.1")])],"isStart":false})],"blendedInto":[makeQuery(id+"F1.opExtrude","CAP_FACE",FACE,{"disambiguationData":[OSD([sQuery(id+"F0.wireOp",EDGE,"E0"),subQ0,sQuery(id+"F0.wireOp",EDGE,"E2.1.0"),sQuery(id+"F0.wireOp",EDGE,"E2.2.0"),sQuery(id+"F0.wireOp",EDGE,"E3"),sQuery(id+"F0.wireOp",EDGE,"E4"),sQuery(id+"F0.wireOp",EDGE,"E6.1.0"),sQuery(id+"F0.wireOp",EDGE,"E6.1.1"),sQuery(id+"F0.wireOp",EDGE,"E6.2.0"),sQuery(id+"F0.wireOp",EDGE,"E6.2.1")])],"isStart":false})]});}
            var Q8;
            {var subQ0=sQuery(id+"F0.wireOp",EDGE,"E6.1.1");Q8=makeQuery(id+"F2.opChamfer","BLEND_EDGE",EDGE,{"blendedFrom":[makeQuery(id+"F1.opExtrude","CAP_EDGE",EDGE,{"disambiguationData":[OSD([subQ0])],"isStart":false}),makeQuery(id+"F1.opExtrude","CAP_FACE",FACE,{"disambiguationData":[OSD([sQuery(id+"F0.wireOp",EDGE,"E0"),sQuery(id+"F0.wireOp",EDGE,"E1"),sQuery(id+"F0.wireOp",EDGE,"E2.1.0"),sQuery(id+"F0.wireOp",EDGE,"E2.2.0"),sQuery(id+"F0.wireOp",EDGE,"E3"),sQuery(id+"F0.wireOp",EDGE,"E4"),sQuery(id+"F0.wireOp",EDGE,"E6.1.0"),subQ0,sQuery(id+"F0.wireOp",EDGE,"E6.2.0"),sQuery(id+"F0.wireOp",EDGE,"E6.2.1")])],"isStart":false})],"blendedInto":[makeQuery(id+"F1.opExtrude","CAP_FACE",FACE,{"disambiguationData":[OSD([sQuery(id+"F0.wireOp",EDGE,"E0"),sQuery(id+"F0.wireOp",EDGE,"E1"),sQuery(id+"F0.wireOp",EDGE,"E2.1.0"),sQuery(id+"F0.wireOp",EDGE,"E2.2.0"),sQuery(id+"F0.wireOp",EDGE,"E3"),sQuery(id+"F0.wireOp",EDGE,"E4"),sQuery(id+"F0.wireOp",EDGE,"E6.1.0"),subQ0,sQuery(id+"F0.wireOp",EDGE,"E6.2.0"),sQuery(id+"F0.wireOp",EDGE,"E6.2.1")])],"isStart":false})]});}
            fillet(context, id + "F5", {"entities" : qUnion([Q0, Q1, Q2, Q3, Q4, Q5, Q6, Q7, Q8]), "radius" : 2.5 * mm, "tangentPropagation" : true, "allowEdgeOverflow" : false});
        }
        {
            var Q0;
            Q0=makeQuery(id+"F4.opFillet","SPLIT",FACE,{"disambiguationData":[OD(1.0)],"derivedFrom":makeQuery(id+"F1.opExtrude","CAP_FACE",FACE,{"disambiguationData":[OSD([sQuery(id+"F0.wireOp",EDGE,"E0"),sQuery(id+"F0.wireOp",EDGE,"E1"),sQuery(id+"F0.wireOp",EDGE,"E2.1.0"),sQuery(id+"F0.wireOp",EDGE,"E2.2.0"),sQuery(id+"F0.wireOp",EDGE,"E3"),sQuery(id+"F0.wireOp",EDGE,"E4"),sQuery(id+"F0.wireOp",EDGE,"E6.1.0"),sQuery(id+"F0.wireOp",EDGE,"E6.1.1"),sQuery(id+"F0.wireOp",EDGE,"E6.2.0"),sQuery(id+"F0.wireOp",EDGE,"E6.2.1")])],"isStart":true})});
            var Q1;
            Q1=makeQuery(id+"F4.opFillet","SPLIT",FACE,{"disambiguationData":[OD(2.0)],"derivedFrom":makeQuery(id+"F1.opExtrude","CAP_FACE",FACE,{"disambiguationData":[OSD([sQuery(id+"F0.wireOp",EDGE,"E0"),sQuery(id+"F0.wireOp",EDGE,"E1"),sQuery(id+"F0.wireOp",EDGE,"E2.1.0"),sQuery(id+"F0.wireOp",EDGE,"E2.2.0"),sQuery(id+"F0.wireOp",EDGE,"E3"),sQuery(id+"F0.wireOp",EDGE,"E4"),sQuery(id+"F0.wireOp",EDGE,"E6.1.0"),sQuery(id+"F0.wireOp",EDGE,"E6.1.1"),sQuery(id+"F0.wireOp",EDGE,"E6.2.0"),sQuery(id+"F0.wireOp",EDGE,"E6.2.1")])],"isStart":true})});
            var Q2;
            Q2=makeQuery(id+"F4.opFillet","SPLIT",FACE,{"disambiguationData":[OD(0.0)],"derivedFrom":makeQuery(id+"F1.opExtrude","CAP_FACE",FACE,{"disambiguationData":[OSD([sQuery(id+"F0.wireOp",EDGE,"E0"),sQuery(id+"F0.wireOp",EDGE,"E1"),sQuery(id+"F0.wireOp",EDGE,"E2.1.0"),sQuery(id+"F0.wireOp",EDGE,"E2.2.0"),sQuery(id+"F0.wireOp",EDGE,"E3"),sQuery(id+"F0.wireOp",EDGE,"E4"),sQuery(id+"F0.wireOp",EDGE,"E6.1.0"),sQuery(id+"F0.wireOp",EDGE,"E6.1.1"),sQuery(id+"F0.wireOp",EDGE,"E6.2.0"),sQuery(id+"F0.wireOp",EDGE,"E6.2.1")])],"isStart":true})});
            fillet(context, id + "F6", {"entities" : qUnion([Q0, Q1, Q2]), "radius" : 1 * mm, "tangentPropagation" : true, "allowEdgeOverflow" : false});
        }
        {
            var Q0;
            Q0=makeQuery(id+"F5.opFillet","SPLIT",FACE,{"disambiguationData":[OD(2.0)],"derivedFrom":makeQuery(id+"F1.opExtrude","CAP_FACE",FACE,{"disambiguationData":[OSD([sQuery(id+"F0.wireOp",EDGE,"E0"),sQuery(id+"F0.wireOp",EDGE,"E1"),sQuery(id+"F0.wireOp",EDGE,"E2.1.0"),sQuery(id+"F0.wireOp",EDGE,"E2.2.0"),sQuery(id+"F0.wireOp",EDGE,"E3"),sQuery(id+"F0.wireOp",EDGE,"E4"),sQuery(id+"F0.wireOp",EDGE,"E6.1.0"),sQuery(id+"F0.wireOp",EDGE,"E6.1.1"),sQuery(id+"F0.wireOp",EDGE,"E6.2.0"),sQuery(id+"F0.wireOp",EDGE,"E6.2.1")])],"isStart":false})});
            var Q1;
            Q1=makeQuery(id+"F5.opFillet","SPLIT",FACE,{"disambiguationData":[OD(1.0)],"derivedFrom":makeQuery(id+"F1.opExtrude","CAP_FACE",FACE,{"disambiguationData":[OSD([sQuery(id+"F0.wireOp",EDGE,"E0"),sQuery(id+"F0.wireOp",EDGE,"E1"),sQuery(id+"F0.wireOp",EDGE,"E2.1.0"),sQuery(id+"F0.wireOp",EDGE,"E2.2.0"),sQuery(id+"F0.wireOp",EDGE,"E3"),sQuery(id+"F0.wireOp",EDGE,"E4"),sQuery(id+"F0.wireOp",EDGE,"E6.1.0"),sQuery(id+"F0.wireOp",EDGE,"E6.1.1"),sQuery(id+"F0.wireOp",EDGE,"E6.2.0"),sQuery(id+"F0.wireOp",EDGE,"E6.2.1")])],"isStart":false})});
            var Q2;
            Q2=makeQuery(id+"F5.opFillet","SPLIT",FACE,{"disambiguationData":[OD(0.0)],"derivedFrom":makeQuery(id+"F1.opExtrude","CAP_FACE",FACE,{"disambiguationData":[OSD([sQuery(id+"F0.wireOp",EDGE,"E0"),sQuery(id+"F0.wireOp",EDGE,"E1"),sQuery(id+"F0.wireOp",EDGE,"E2.1.0"),sQuery(id+"F0.wireOp",EDGE,"E2.2.0"),sQuery(id+"F0.wireOp",EDGE,"E3"),sQuery(id+"F0.wireOp",EDGE,"E4"),sQuery(id+"F0.wireOp",EDGE,"E6.1.0"),sQuery(id+"F0.wireOp",EDGE,"E6.1.1"),sQuery(id+"F0.wireOp",EDGE,"E6.2.0"),sQuery(id+"F0.wireOp",EDGE,"E6.2.1")])],"isStart":false})});
            fillet(context, id + "F7", {"entities" : qUnion([Q0, Q1, Q2]), "radius" : 1 * mm, "tangentPropagation" : true, "allowEdgeOverflow" : false});
        }
    });
